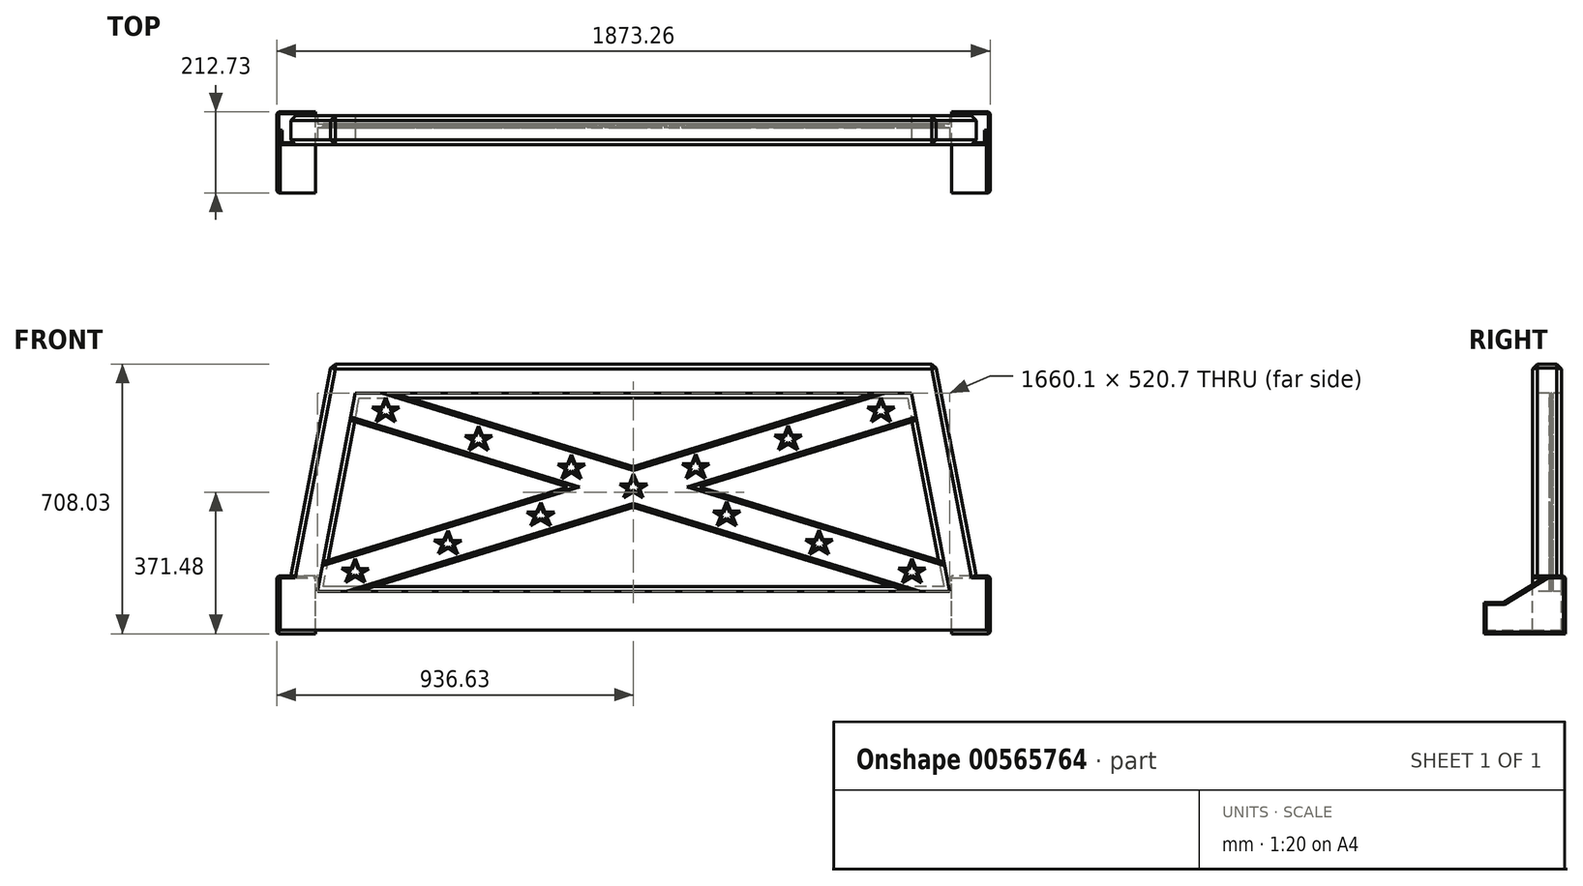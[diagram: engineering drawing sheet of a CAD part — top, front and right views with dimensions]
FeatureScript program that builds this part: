
annotation { "Feature Type Name" : "Feature", "Feature Type Description" : "" }
export const myFeature = defineFeature(function(context is Context, id is Id, definition is map)
    precondition{}
    {
        {
            var Q0;
            Q0=qCreatedBy(makeId("Front.planeOp"),FACE);
            var sketch = newSketch(context, id + "F0", { "sketchPlane" : qUnion([Q0])});
            skLineSegment(sketch, "E0", {"start": v(0, 0) * mm, "end": v(1854.2, 0) * mm});
            skLineSegment(sketch, "E1", {"start": v(0, 0) * mm, "end": v(133.8, 698.5) * mm});
            skLineSegment(sketch, "E2", {"start": v(1854.2, 0) * mm, "end": v(1720.4, 698.5) * mm});
            skLineSegment(sketch, "E3", {"start": v(133.8, 698.5) * mm, "end": v(1720.4, 698.5) * mm});
            skSolve(sketch);
        }
        {
            var Q0;
            Q0=makeQuery(id+"F0.imprint","IMPRINT",FACE,{"disambiguationData":[TD([[makeQuery(id+"F0.imprint","IMPRINT",EDGE,{"derivedFrom":sQuery(id+"F0.wireOp",EDGE,"E0")}),1.0]])]});
            var Q1;
            Q1 = qSketchRegion(id + "F2", true);
            extrude(context, id + "F1", {"entities" : qUnion([Q0, Q1]), "depth" : 76.2 * mm, "offsetDistance" : 25.4 * mm});
        }
        {
            var Q0;
            Q0=qCreatedBy(makeId("Front.planeOp"),FACE);
            var sketch = newSketch(context, id + "F2", { "sketchPlane" : qUnion([Q0])});
            skLineSegment(sketch, "E4.bottom", {"start": v(-9.53, -9.53) * mm, "end": v(92.08, -9.53) * mm});
            skLineSegment(sketch, "E4.top", {"start": v(-9.53, 142.88) * mm, "end": v(92.07, 142.88) * mm});
            skLineSegment(sketch, "E4.left", {"start": v(-9.52, -9.53) * mm, "end": v(-9.53, 142.88) * mm});
            skLineSegment(sketch, "E4.right", {"start": v(92.08, -9.53) * mm, "end": v(92.07, 142.88) * mm});
            skLineSegment(sketch, "E5.bottom", {"start": v(1863.73, -9.52) * mm, "end": v(1762.13, -9.52) * mm});
            skLineSegment(sketch, "E5.top", {"start": v(1863.73, 142.88) * mm, "end": v(1762.13, 142.88) * mm});
            skLineSegment(sketch, "E5.left", {"start": v(1863.73, -9.52) * mm, "end": v(1863.73, 142.88) * mm});
            skLineSegment(sketch, "E5.right", {"start": v(1762.13, -9.52) * mm, "end": v(1762.13, 142.88) * mm});
            skSolve(sketch);
        }
        {
            var Q0;
            Q0 = qSketchRegion(id + "F2", true);
            extrude(context, id + "F3", {"entities" : qUnion([Q0]), "operationType" : NewBodyOperationType.ADD, "oppositeDirection" : true, "depth" : 9.52 * mm, "offsetDistance" : 25.4 * mm});
        }
        {
            var Q0;
            Q0=qCreatedBy(makeId("Front.planeOp"),FACE);
            var sketch = newSketch(context, id + "F4", { "sketchPlane" : qUnion([Q0])});
            skLineSegment(sketch, "E6", {"start": v(92.08, 0) * mm, "end": v(92.08, -9.53) * mm});
            skLineSegment(sketch, "E7", {"start": v(92.08, -9.53) * mm, "end": v(-9.52, -9.53) * mm});
            skLineSegment(sketch, "E8", {"start": v(-9.52, -9.53) * mm, "end": v(-9.52, 142.87) * mm});
            skLineSegment(sketch, "E9", {"start": v(-9.52, 142.87) * mm, "end": v(0, 142.87) * mm});
            skLineSegment(sketch, "E10", {"start": v(0, 142.87) * mm, "end": v(0, 0) * mm});
            skLineSegment(sketch, "E11", {"start": v(0, 0) * mm, "end": v(92.08, 0) * mm});
            skLineSegment(sketch, "E12", {"start": v(1863.73, -9.52) * mm, "end": v(1863.73, 142.88) * mm});
            skLineSegment(sketch, "E13", {"start": v(1863.73, 142.88) * mm, "end": v(1854.2, 142.88) * mm});
            skLineSegment(sketch, "E14", {"start": v(1854.2, 142.88) * mm, "end": v(1854.2, 0) * mm});
            skLineSegment(sketch, "E15", {"start": v(1854.2, 0) * mm, "end": v(1762.13, 0) * mm});
            skLineSegment(sketch, "E16", {"start": v(1762.13, 0) * mm, "end": v(1762.13, -9.53) * mm});
            skLineSegment(sketch, "E17", {"start": v(1762.13, -9.53) * mm, "end": v(1863.73, -9.52) * mm});
            skSolve(sketch);
        }
        {
            var Q0;
            Q0 = qSketchRegion(id + "F4", true);
            var Q1;
            Q1 = qSketchRegion(id + "F6", true);
            extrude(context, id + "F5", {"entities" : qUnion([Q0, Q1]), "operationType" : NewBodyOperationType.ADD, "depth" : 152.4 * mm, "offsetDistance" : 25.4 * mm});
        }
        {
            var Q0;
            Q0=qCreatedBy(makeId("Right.planeOp"),FACE);
            var sketch = newSketch(context, id + "F6", { "sketchPlane" : qUnion([Q0])});
            skLineSegment(sketch, "E18", {"start": v(-38.1, 142.88) * mm, "end": v(-152.4, 73.02) * mm});
            skLineSegment(sketch, "E19", {"start": v(-152.4, 73.02) * mm, "end": v(-152.4, 142.88) * mm});
            skLineSegment(sketch, "E20", {"start": v(-152.4, 142.88) * mm, "end": v(-38.1, 142.88) * mm});
            skSolve(sketch);
        }
        {
            var Q0;
            Q0 = qSketchRegion(id + "F6", true);
            extrude(context, id + "F7", {"entities" : qUnion([Q0]), "operationType" : NewBodyOperationType.REMOVE, "oppositeDirection" : true, "depth" : 9.52 * mm, "offsetDistance" : 25.4 * mm});
        }
        {
            var Q0;
            Q0=makeQuery(id+"F5.opExtrude","SWEPT_FACE",FACE,{"disambiguationData":[OSD([sQuery(id+"F4.wireOp",EDGE,"E14")])]});
            var sketch = newSketch(context, id + "F8", { "sketchPlane" : qUnion([Q0])});
            skLineSegment(sketch, "E21", {"start": v(38.1, 142.87) * mm, "end": v(152.4, 73.02) * mm});
            skLineSegment(sketch, "E22", {"start": v(152.4, 73.02) * mm, "end": v(152.4, 142.87) * mm});
            skLineSegment(sketch, "E23", {"start": v(152.4, 142.87) * mm, "end": v(38.1, 142.87) * mm});
            skSolve(sketch);
        }
        {
            var Q0;
            Q0 = qSketchRegion(id + "F8", true);
            extrude(context, id + "F9", {"entities" : qUnion([Q0]), "operationType" : NewBodyOperationType.REMOVE, "oppositeDirection" : true, "depth" : 9.52 * mm, "offsetDistance" : 25.4 * mm});
        }
        {
            var Q0;
            Q0=makeQuery(id+"F5.opExtrude","CAP_FACE",FACE,{"disambiguationData":[OSD([sQuery(id+"F4.wireOp",EDGE,"E12"),sQuery(id+"F4.wireOp",EDGE,"E13"),sQuery(id+"F4.wireOp",EDGE,"E14"),sQuery(id+"F4.wireOp",EDGE,"E15"),sQuery(id+"F4.wireOp",EDGE,"E16"),sQuery(id+"F4.wireOp",EDGE,"E17")])],"isStart":false});
            var sketch = newSketch(context, id + "F10", { "sketchPlane" : qUnion([Q0])});
            skLineSegment(sketch, "E24", {"start": v(1762.13, -9.53) * mm, "end": v(1863.73, -9.52) * mm});
            skLineSegment(sketch, "E25", {"start": v(1863.73, -9.52) * mm, "end": v(1863.73, 73.03) * mm});
            skLineSegment(sketch, "E26", {"start": v(1863.73, 73.03) * mm, "end": v(1854.2, 73.03) * mm});
            skLineSegment(sketch, "E27", {"start": v(1854.2, 73.03) * mm, "end": v(1854.2, 0) * mm});
            skLineSegment(sketch, "E28", {"start": v(1854.2, 0) * mm, "end": v(1762.13, 0) * mm});
            skLineSegment(sketch, "E29", {"start": v(1762.13, 0) * mm, "end": v(1762.13, -9.53) * mm});
            skSolve(sketch);
        }
        {
            var Q0;
            Q0 = qSketchRegion(id + "F10", true);
            var Q1;
            Q1 = qSketchRegion(id + "F12", true);
            extrude(context, id + "F11", {"entities" : qUnion([Q0, Q1]), "operationType" : NewBodyOperationType.ADD, "depth" : 50.8 * mm, "offsetDistance" : 25.4 * mm});
        }
        {
            var Q0;
            Q0=makeQuery(id+"F5.opExtrude","CAP_FACE",FACE,{"disambiguationData":[OSD([sQuery(id+"F4.wireOp",EDGE,"E6"),sQuery(id+"F4.wireOp",EDGE,"E7"),sQuery(id+"F4.wireOp",EDGE,"E8"),sQuery(id+"F4.wireOp",EDGE,"E9"),sQuery(id+"F4.wireOp",EDGE,"E10"),sQuery(id+"F4.wireOp",EDGE,"E11")])],"isStart":false});
            var sketch = newSketch(context, id + "F12", { "sketchPlane" : qUnion([Q0])});
            skLineSegment(sketch, "E30", {"start": v(-9.52, 73.02) * mm, "end": v(0, 73.02) * mm});
            skLineSegment(sketch, "E31", {"start": v(0, 73.02) * mm, "end": v(0, 0) * mm});
            skLineSegment(sketch, "E32", {"start": v(0, 0) * mm, "end": v(92.08, 0) * mm});
            skLineSegment(sketch, "E33", {"start": v(92.08, 0) * mm, "end": v(92.08, -9.53) * mm});
            skLineSegment(sketch, "E34", {"start": v(92.08, -9.53) * mm, "end": v(-9.52, -9.53) * mm});
            skLineSegment(sketch, "E35", {"start": v(-9.52, -9.52) * mm, "end": v(-9.52, 73.02) * mm});
            skSolve(sketch);
        }
        {
            var Q0;
            Q0 = qSketchRegion(id + "F12", true);
            extrude(context, id + "F13", {"entities" : qUnion([Q0]), "operationType" : NewBodyOperationType.ADD, "depth" : 50.8 * mm, "offsetDistance" : 25.4 * mm});
        }
        {
            var Q0;
            Q0=makeQuery(id+"F1.opExtrude","CAP_FACE",FACE,{"disambiguationData":[OSD([sQuery(id+"F0.wireOp",EDGE,"E0"),sQuery(id+"F0.wireOp",EDGE,"E1"),sQuery(id+"F0.wireOp",EDGE,"E2"),sQuery(id+"F0.wireOp",EDGE,"E3")])],"isStart":false});
            var sketch = newSketch(context, id + "F14", { "sketchPlane" : qUnion([Q0])});
            skLineSegment(sketch, "E36", {"start": v(97.05, 101.6) * mm, "end": v(196.8, 622.3) * mm});
            skLineSegment(sketch, "E37", {"start": v(196.8, 622.3) * mm, "end": v(1657.4, 622.3) * mm});
            skLineSegment(sketch, "E38", {"start": v(1657.4, 622.3) * mm, "end": v(1757.15, 101.6) * mm});
            skLineSegment(sketch, "E39", {"start": v(1757.15, 101.6) * mm, "end": v(97.05, 101.6) * mm});
            skSolve(sketch);
        }
        {
            var Q0;
            Q0=makeQuery(id+"F14.imprint","IMPRINT",FACE,{"disambiguationData":[TD([[makeQuery(id+"F14.imprint","IMPRINT",EDGE,{"derivedFrom":sQuery(id+"F14.wireOp",EDGE,"E36")}),-1.0]])]});
            extrude(context, id + "F15", {"entities" : qUnion([Q0]), "operationType" : NewBodyOperationType.REMOVE, "oppositeDirection" : true, "depth" : 76.2 * mm, "offsetDistance" : 25.4 * mm});
        }
        {
            var Q0;
            Q0=makeQuery(id+"F1.opExtrude","CAP_FACE",FACE,{"disambiguationData":[OSD([sQuery(id+"F0.wireOp",EDGE,"E0"),sQuery(id+"F0.wireOp",EDGE,"E1"),sQuery(id+"F0.wireOp",EDGE,"E2"),sQuery(id+"F0.wireOp",EDGE,"E3")])],"isStart":false});
            cPlane(context, id + "F16", {"entities" : qUnion([Q0]), "cplaneType" : CPlaneType.OFFSET, "offset" : 50.8 * mm, "oppositeDirection" : true, "width" : 152.4 * mm, "height" : 152.4 * mm});
        }
        {
            var Q0;
            Q0=qCreatedBy(id+"F16.planeOp",FACE);
            var sketch = newSketch(context, id + "F17", { "sketchPlane" : qUnion([Q0])});
            skLineSegment(sketch, "E40", {"start": v(97.05, 101.6) * mm, "end": v(196.8, 622.3) * mm});
            skLineSegment(sketch, "E41", {"start": v(196.8, 622.3) * mm, "end": v(1657.4, 622.3) * mm});
            skLineSegment(sketch, "E42", {"start": v(1657.4, 622.3) * mm, "end": v(1757.15, 101.6) * mm});
            skLineSegment(sketch, "E43", {"start": v(1757.15, 101.6) * mm, "end": v(97.05, 101.6) * mm});
            skLineSegment(sketch, "E44", {"start": v(112.41, 114.3) * mm, "end": v(207.29, 609.6) * mm});
            skLineSegment(sketch, "E45", {"start": v(207.29, 609.6) * mm, "end": v(1646.91, 609.6) * mm});
            skLineSegment(sketch, "E46", {"start": v(1646.91, 609.6) * mm, "end": v(1741.79, 114.3) * mm});
            skLineSegment(sketch, "E47", {"start": v(1741.79, 114.3) * mm, "end": v(112.41, 114.3) * mm});
            skSolve(sketch);
        }
        {
            var Q0;
            Q0 = qSketchRegion(id + "F17", true);
            extrude(context, id + "F18", {"entities" : qUnion([Q0]), "operationType" : NewBodyOperationType.ADD, "oppositeDirection" : true, "depth" : 3.17 * mm, "offsetDistance" : 25.4 * mm});
        }
        {
            var Q0;
            Q0=qCreatedBy(id+"F16.planeOp",FACE);
            var sketch = newSketch(context, id + "F19", { "sketchPlane" : qUnion([Q0])});
            skLineSegment(sketch, "E48", {"start": v(97.05, 101.6) * mm, "end": v(196.8, 622.3) * mm});
            skLineSegment(sketch, "E49", {"start": v(196.8, 622.3) * mm, "end": v(1657.4, 622.3) * mm});
            skLineSegment(sketch, "E50", {"start": v(1657.4, 622.3) * mm, "end": v(1757.15, 101.6) * mm});
            skLineSegment(sketch, "E51", {"start": v(1757.15, 101.6) * mm, "end": v(97.05, 101.6) * mm});
            skSolve(sketch);
        }
        {
            var Q0;
            Q0=qCreatedBy(id+"F16.planeOp",FACE);
            var sketch = newSketch(context, id + "F20", { "sketchPlane" : qUnion([Q0])});
            skLineSegment(sketch, "E52", {"start": v(196.8, 622.3) * mm, "end": v(97.05, 101.6) * mm});
            skLineSegment(sketch, "E53", {"start": v(97.05, 101.6) * mm, "end": v(1757.15, 101.6) * mm});
            skLineSegment(sketch, "E54", {"start": v(1757.15, 101.6) * mm, "end": v(1657.4, 622.3) * mm});
            skLineSegment(sketch, "E55", {"start": v(1657.4, 622.3) * mm, "end": v(196.8, 622.3) * mm});
            skSolve(sketch);
        }
        {
            var Q0;
            Q0 = qSketchRegion(id + "F20", true);
            var Q1;
            Q1 = qSketchRegion(id + "FLFXTix34sU0pSf_1", true);
            extrude(context, id + "F21", {"entities" : qUnion([Q0, Q1]), "operationType" : NewBodyOperationType.ADD, "depth" : 3.17 * mm, "offsetDistance" : 25.4 * mm});
        }
        {
            var Q0;
            Q0=makeQuery(id+"F21.opExtrude","CAP_FACE",FACE,{"disambiguationData":[OSD([sQuery(id+"F20.wireOp",EDGE,"E52"),sQuery(id+"F20.wireOp",EDGE,"E53"),sQuery(id+"F20.wireOp",EDGE,"E54"),sQuery(id+"F20.wireOp",EDGE,"E55")])],"isStart":false});
            var sketch = newSketch(context, id + "F22", { "sketchPlane" : qUnion([Q0])});
            skLineSegment(sketch, "E56", {"start": v(183.2, 551.37) * mm, "end": v(753.9, 376.28) * mm});
            skLineSegment(sketch, "E57", {"start": v(298.4, 622.3) * mm, "end": v(927.1, 429.41) * mm});
            skLineSegment(sketch, "E58", {"start": v(111.94, 179.32) * mm, "end": v(753.9, 376.28) * mm});
            skLineSegment(sketch, "E59", {"start": v(205, 101.6) * mm, "end": v(927.1, 323.14) * mm});
            skLineSegment(sketch, "E60.trimOffspring", {"start": v(927.1, 429.41) * mm, "end": v(1555.8, 622.3) * mm});
            skLineSegment(sketch, "E61.trimOffspring", {"start": v(1100.3, 376.28) * mm, "end": v(1742.26, 179.32) * mm});
            skLineSegment(sketch, "E62.trimOffspring", {"start": v(1100.3, 376.28) * mm, "end": v(1671, 551.37) * mm});
            skLineSegment(sketch, "E63.trimOffspring", {"start": v(927.1, 323.14) * mm, "end": v(1649.2, 101.6) * mm});
            skSolve(sketch);
        }
        {
            var Q0;
            {var subQ0=sQuery(id+"F22.wireOp",EDGE,"E56");Q0=makeQuery(id+"F22.imprint","IMPRINT",FACE,{"disambiguationData":[TD([[makeQuery(id+"F22.imprint","IMPRINT",EDGE,{"derivedFrom":subQ0}),-1.0]])]});}
            var Q1;
            {var subQ0=sQuery(id+"F22.wireOp",EDGE,"E57");Q1=makeQuery(id+"F22.imprint","IMPRINT",FACE,{"disambiguationData":[TD([[makeQuery(id+"F22.imprint","IMPRINT",EDGE,{"derivedFrom":subQ0}),1.0]])]});}
            var Q2;
            {var subQ0=sQuery(id+"F22.wireOp",EDGE,"E61.trimOffspring");Q2=makeQuery(id+"F22.imprint","IMPRINT",FACE,{"disambiguationData":[TD([[makeQuery(id+"F22.imprint","IMPRINT",EDGE,{"derivedFrom":subQ0}),1.0]])]});}
            var Q3;
            {var subQ0=sQuery(id+"F22.wireOp",EDGE,"E59");Q3=makeQuery(id+"F22.imprint","IMPRINT",FACE,{"disambiguationData":[TD([[makeQuery(id+"F22.imprint","IMPRINT",EDGE,{"derivedFrom":subQ0}),-1.0]])]});}
            extrude(context, id + "F23", {"entities" : qUnion([Q0, Q1, Q2, Q3]), "operationType" : NewBodyOperationType.REMOVE, "oppositeDirection" : true, "depth" : 3.17 * mm, "offsetDistance" : 25.4 * mm});
        }
        {
            var Q0;
            Q0=makeQuery(id+"F21.opExtrude","CAP_FACE",FACE,{"disambiguationData":[OSD([sQuery(id+"F20.wireOp",EDGE,"E52"),sQuery(id+"F20.wireOp",EDGE,"E53"),sQuery(id+"F20.wireOp",EDGE,"E54"),sQuery(id+"F20.wireOp",EDGE,"E55")])],"isStart":false});
            var sketch = newSketch(context, id + "F24", { "sketchPlane" : qUnion([Q0])});
            skLineSegment(sketch, "E64", {"start": v(184.4, 557.64) * mm, "end": v(775.55, 376.28) * mm});
            skLineSegment(sketch, "E65", {"start": v(775.55, 376.28) * mm, "end": v(110.58, 172.27) * mm});
            skLineSegment(sketch, "E66", {"start": v(183.35, 101.6) * mm, "end": v(927.1, 329.78) * mm});
            skLineSegment(sketch, "E67", {"start": v(927.1, 329.78) * mm, "end": v(1670.85, 101.6) * mm});
            skLineSegment(sketch, "E68", {"start": v(276.74, 622.3) * mm, "end": v(927.1, 422.77) * mm});
            skLineSegment(sketch, "E69", {"start": v(927.1, 422.77) * mm, "end": v(1577.46, 622.3) * mm});
            skLineSegment(sketch, "E70", {"start": v(1669.8, 557.64) * mm, "end": v(1078.65, 376.28) * mm});
            skLineSegment(sketch, "E71", {"start": v(1078.65, 376.28) * mm, "end": v(1743.62, 172.27) * mm});
            skSolve(sketch);
        }
        {
            var Q0;
            {var subQ30=sQuery(id+"F24.wireOp",EDGE,"E64");Q0=makeQuery(id+"F24.imprint","IMPRINT",FACE,{"disambiguationData":[TD([[makeQuery(id+"F24.imprint","IMPRINT",EDGE,{"derivedFrom":subQ30}),1.0]])]});}
            extrude(context, id + "F25", {"entities" : qUnion([Q0]), "operationType" : NewBodyOperationType.ADD, "depth" : 3.17 * mm, "offsetDistance" : 25.4 * mm});
        }
        {
            var Q0;
            Q0=makeQuery(id+"F25.opExtrude","CAP_FACE",FACE,{"disambiguationData":[OSD([sQuery(id+"F20.wireOp",EDGE,"E52"),sQuery(id+"F20.wireOp",EDGE,"E53"),sQuery(id+"F20.wireOp",EDGE,"E54"),sQuery(id+"F20.wireOp",EDGE,"E55"),sQuery(id+"F24.wireOp",EDGE,"E64"),sQuery(id+"F24.wireOp",EDGE,"E65"),sQuery(id+"F24.wireOp",EDGE,"E66"),sQuery(id+"F24.wireOp",EDGE,"E67"),sQuery(id+"F24.wireOp",EDGE,"E68"),sQuery(id+"F24.wireOp",EDGE,"E69"),sQuery(id+"F24.wireOp",EDGE,"E70"),sQuery(id+"F24.wireOp",EDGE,"E71")])],"isStart":false});
            var sketch = newSketch(context, id + "F26", { "sketchPlane" : qUnion([Q0])});
            skLineSegment(sketch, "E72", {"start": v(241.55, 585.93) * mm, "end": v(266.95, 585.93) * mm});
            skLineSegment(sketch, "E73", {"start": v(312.67, 585.93) * mm, "end": v(292.35, 573.23) * mm});
            skLineSegment(sketch, "E74", {"start": v(251.7, 547.83) * mm, "end": v(261.87, 573.23) * mm});
            skLineSegment(sketch, "E75", {"start": v(277.1, 611.33) * mm, "end": v(287.27, 585.93) * mm});
            skLineSegment(sketch, "E76", {"start": v(302.5, 547.83) * mm, "end": v(277.1, 563.7) * mm});
            skLineSegment(sketch, "E77.trimOffspring", {"start": v(266.95, 585.93) * mm, "end": v(277.1, 611.33) * mm});
            skLineSegment(sketch, "E78.trimOffspring", {"start": v(287.27, 585.93) * mm, "end": v(312.67, 585.93) * mm});
            skLineSegment(sketch, "E79.trimOffspring", {"start": v(292.35, 573.23) * mm, "end": v(302.5, 547.83) * mm});
            skLineSegment(sketch, "E80.trimOffspring", {"start": v(277.1, 563.7) * mm, "end": v(251.7, 547.83) * mm});
            skLineSegment(sketch, "E81.trimOffspring", {"start": v(261.87, 573.23) * mm, "end": v(241.55, 585.93) * mm});
            skLineSegment(sketch, "E82.1.0.0", {"start": v(556, 511.05) * mm, "end": v(535.69, 498.35) * mm});
            skLineSegment(sketch, "E82.1.0.1", {"start": v(530.6, 511.05) * mm, "end": v(556, 511.05) * mm});
            skLineSegment(sketch, "E82.1.0.2", {"start": v(520.45, 536.45) * mm, "end": v(530.6, 511.05) * mm});
            skLineSegment(sketch, "E82.1.0.3", {"start": v(510.29, 511.05) * mm, "end": v(520.45, 536.45) * mm});
            skLineSegment(sketch, "E82.1.0.4", {"start": v(484.89, 511.05) * mm, "end": v(510.29, 511.05) * mm});
            skLineSegment(sketch, "E82.1.0.5", {"start": v(505.2, 498.35) * mm, "end": v(484.89, 511.05) * mm});
            skLineSegment(sketch, "E82.1.0.6", {"start": v(535.69, 498.35) * mm, "end": v(545.85, 472.95) * mm});
            skLineSegment(sketch, "E82.1.0.7", {"start": v(545.85, 472.95) * mm, "end": v(520.45, 488.82) * mm});
            skLineSegment(sketch, "E82.1.0.8", {"start": v(520.45, 488.82) * mm, "end": v(495.05, 472.95) * mm});
            skLineSegment(sketch, "E82.1.0.9", {"start": v(495.05, 472.95) * mm, "end": v(505.2, 498.35) * mm});
            skLineSegment(sketch, "E82.2.0.0", {"start": v(799.34, 436.16) * mm, "end": v(779.02, 423.46) * mm});
            skLineSegment(sketch, "E82.2.0.1", {"start": v(773.94, 436.16) * mm, "end": v(799.34, 436.16) * mm});
            skLineSegment(sketch, "E82.2.0.2", {"start": v(763.78, 461.56) * mm, "end": v(773.94, 436.16) * mm});
            skLineSegment(sketch, "E82.2.0.3", {"start": v(753.62, 436.16) * mm, "end": v(763.78, 461.56) * mm});
            skLineSegment(sketch, "E82.2.0.4", {"start": v(728.22, 436.16) * mm, "end": v(753.62, 436.16) * mm});
            skLineSegment(sketch, "E82.2.0.5", {"start": v(748.54, 423.46) * mm, "end": v(728.22, 436.16) * mm});
            skLineSegment(sketch, "E82.2.0.6", {"start": v(779.02, 423.46) * mm, "end": v(789.18, 398.06) * mm});
            skLineSegment(sketch, "E82.2.0.7", {"start": v(789.18, 398.06) * mm, "end": v(763.78, 413.94) * mm});
            skLineSegment(sketch, "E82.2.0.8", {"start": v(763.78, 413.94) * mm, "end": v(738.38, 398.06) * mm});
            skLineSegment(sketch, "E82.2.0.9", {"start": v(738.38, 398.06) * mm, "end": v(748.54, 423.46) * mm});
            skLineSegment(sketch, "E82.direction1", {"start": v(292.35, 573.23) * mm, "end": v(535.69, 498.35) * mm, "construction": true});
            skLineSegment(sketch, "E83.2.0.0", {"start": v(232.58, 161.52) * mm, "end": v(212.63, 149.52) * mm});
            skLineSegment(sketch, "E83.2.0.1", {"start": v(207.18, 161.52) * mm, "end": v(232.58, 161.52) * mm});
            skLineSegment(sketch, "E83.2.0.2", {"start": v(196.66, 187.82) * mm, "end": v(207.18, 161.52) * mm});
            skLineSegment(sketch, "E83.2.0.3", {"start": v(185.78, 162.2) * mm, "end": v(196.66, 187.82) * mm});
            skLineSegment(sketch, "E83.2.0.4", {"start": v(160.38, 162.2) * mm, "end": v(185.78, 162.2) * mm});
            skLineSegment(sketch, "E83.2.0.5", {"start": v(181.19, 149.52) * mm, "end": v(160.38, 162.2) * mm});
            skLineSegment(sketch, "E83.2.0.6", {"start": v(212.63, 149.52) * mm, "end": v(222.06, 125.93) * mm});
            skLineSegment(sketch, "E83.2.0.7", {"start": v(222.06, 125.93) * mm, "end": v(196.66, 141.42) * mm});
            skLineSegment(sketch, "E83.2.0.8", {"start": v(196.66, 141.42) * mm, "end": v(171.26, 126.14) * mm});
            skLineSegment(sketch, "E83.2.0.9", {"start": v(171.26, 126.14) * mm, "end": v(181.19, 149.52) * mm});
            skLineSegment(sketch, "E84.1.0.0", {"start": v(429.26, 236.22) * mm, "end": v(440.14, 261.84) * mm});
            skLineSegment(sketch, "E84.1.0.1", {"start": v(450.66, 235.54) * mm, "end": v(476.06, 235.54) * mm});
            skLineSegment(sketch, "E84.1.0.2", {"start": v(440.14, 261.84) * mm, "end": v(450.66, 235.54) * mm});
            skLineSegment(sketch, "E84.1.0.3", {"start": v(476.06, 235.54) * mm, "end": v(456.1, 223.54) * mm});
            skLineSegment(sketch, "E84.1.0.4", {"start": v(456.1, 223.54) * mm, "end": v(465.54, 199.95) * mm});
            skLineSegment(sketch, "E84.1.0.5", {"start": v(465.54, 199.95) * mm, "end": v(440.14, 215.44) * mm});
            skLineSegment(sketch, "E84.1.0.6", {"start": v(440.14, 215.44) * mm, "end": v(414.74, 200.16) * mm});
            skLineSegment(sketch, "E84.1.0.7", {"start": v(414.74, 200.16) * mm, "end": v(424.67, 223.54) * mm});
            skLineSegment(sketch, "E84.1.0.8", {"start": v(424.67, 223.54) * mm, "end": v(403.86, 236.22) * mm});
            skLineSegment(sketch, "E84.1.0.9", {"start": v(403.86, 236.22) * mm, "end": v(429.26, 236.22) * mm});
            skLineSegment(sketch, "E84.2.0.0", {"start": v(672.74, 310.24) * mm, "end": v(683.62, 335.86) * mm});
            skLineSegment(sketch, "E84.2.0.1", {"start": v(694.14, 309.56) * mm, "end": v(719.54, 309.56) * mm});
            skLineSegment(sketch, "E84.2.0.2", {"start": v(683.62, 335.86) * mm, "end": v(694.14, 309.56) * mm});
            skLineSegment(sketch, "E84.2.0.3", {"start": v(719.54, 309.56) * mm, "end": v(699.59, 297.56) * mm});
            skLineSegment(sketch, "E84.2.0.4", {"start": v(699.59, 297.56) * mm, "end": v(709.02, 273.97) * mm});
            skLineSegment(sketch, "E84.2.0.5", {"start": v(709.02, 273.97) * mm, "end": v(683.62, 289.46) * mm});
            skLineSegment(sketch, "E84.2.0.6", {"start": v(683.62, 289.46) * mm, "end": v(658.22, 274.18) * mm});
            skLineSegment(sketch, "E84.2.0.7", {"start": v(658.22, 274.18) * mm, "end": v(668.15, 297.56) * mm});
            skLineSegment(sketch, "E84.2.0.8", {"start": v(668.15, 297.56) * mm, "end": v(647.34, 310.24) * mm});
            skLineSegment(sketch, "E84.2.0.9", {"start": v(647.34, 310.24) * mm, "end": v(672.74, 310.24) * mm});
            skLineSegment(sketch, "E84.3.0.0", {"start": v(916.22, 384.26) * mm, "end": v(927.1, 409.88) * mm});
            skLineSegment(sketch, "E84.3.0.1", {"start": v(937.62, 383.58) * mm, "end": v(963.02, 383.58) * mm});
            skLineSegment(sketch, "E84.3.0.2", {"start": v(927.1, 409.88) * mm, "end": v(937.62, 383.58) * mm});
            skLineSegment(sketch, "E84.3.0.3", {"start": v(963.02, 383.58) * mm, "end": v(943.07, 371.58) * mm});
            skLineSegment(sketch, "E84.3.0.4", {"start": v(943.07, 371.58) * mm, "end": v(952.5, 348) * mm});
            skLineSegment(sketch, "E84.3.0.5", {"start": v(952.5, 348) * mm, "end": v(927.1, 363.48) * mm});
            skLineSegment(sketch, "E84.3.0.6", {"start": v(927.1, 363.48) * mm, "end": v(901.7, 348.2) * mm});
            skLineSegment(sketch, "E84.3.0.7", {"start": v(901.7, 348.2) * mm, "end": v(911.63, 371.58) * mm});
            skLineSegment(sketch, "E84.3.0.8", {"start": v(911.63, 371.58) * mm, "end": v(890.82, 384.26) * mm});
            skLineSegment(sketch, "E84.3.0.9", {"start": v(890.82, 384.26) * mm, "end": v(916.22, 384.26) * mm});
            skLineSegment(sketch, "E84.direction1", {"start": v(185.78, 162.2) * mm, "end": v(429.26, 236.22) * mm, "construction": true});
            skLineSegment(sketch, "E85.2.0.0", {"start": v(1612.65, 585.94) * mm, "end": v(1592.33, 573.24) * mm});
            skLineSegment(sketch, "E85.2.0.1", {"start": v(1587.25, 585.94) * mm, "end": v(1612.65, 585.94) * mm});
            skLineSegment(sketch, "E85.2.0.2", {"start": v(1577.09, 611.34) * mm, "end": v(1587.25, 585.94) * mm});
            skLineSegment(sketch, "E85.2.0.3", {"start": v(1566.93, 585.94) * mm, "end": v(1577.09, 611.34) * mm});
            skLineSegment(sketch, "E85.2.0.4", {"start": v(1541.53, 585.94) * mm, "end": v(1566.93, 585.94) * mm});
            skLineSegment(sketch, "E85.2.0.5", {"start": v(1561.85, 573.24) * mm, "end": v(1541.53, 585.94) * mm});
            skLineSegment(sketch, "E85.2.0.6", {"start": v(1592.33, 573.24) * mm, "end": v(1602.49, 547.84) * mm});
            skLineSegment(sketch, "E85.2.0.7", {"start": v(1602.49, 547.84) * mm, "end": v(1577.09, 563.72) * mm});
            skLineSegment(sketch, "E85.2.0.8", {"start": v(1577.09, 563.72) * mm, "end": v(1551.69, 547.84) * mm});
            skLineSegment(sketch, "E85.2.0.9", {"start": v(1551.69, 547.84) * mm, "end": v(1561.85, 573.24) * mm});
            skLineSegment(sketch, "E86.2.0.0", {"start": v(1693.82, 162.2) * mm, "end": v(1673.5, 149.5) * mm});
            skLineSegment(sketch, "E86.2.0.1", {"start": v(1668.42, 162.2) * mm, "end": v(1693.82, 162.2) * mm});
            skLineSegment(sketch, "E86.2.0.2", {"start": v(1658.26, 187.6) * mm, "end": v(1668.42, 162.2) * mm});
            skLineSegment(sketch, "E86.2.0.3", {"start": v(1648.1, 162.2) * mm, "end": v(1658.26, 187.6) * mm});
            skLineSegment(sketch, "E86.2.0.4", {"start": v(1622.7, 162.2) * mm, "end": v(1648.1, 162.2) * mm});
            skLineSegment(sketch, "E86.2.0.5", {"start": v(1643.02, 149.5) * mm, "end": v(1622.7, 162.2) * mm});
            skLineSegment(sketch, "E86.2.0.6", {"start": v(1673.5, 149.5) * mm, "end": v(1683.66, 124.1) * mm});
            skLineSegment(sketch, "E86.2.0.7", {"start": v(1683.66, 124.1) * mm, "end": v(1658.26, 139.98) * mm});
            skLineSegment(sketch, "E86.2.0.8", {"start": v(1658.26, 139.98) * mm, "end": v(1632.86, 124.1) * mm});
            skLineSegment(sketch, "E86.2.0.9", {"start": v(1632.86, 124.1) * mm, "end": v(1643.02, 149.5) * mm});
            skLineSegment(sketch, "E87.1.0.0", {"start": v(1415.1, 215.05) * mm, "end": v(1389.7, 199.17) * mm});
            skLineSegment(sketch, "E87.1.0.1", {"start": v(1440.5, 199.17) * mm, "end": v(1415.1, 215.05) * mm});
            skLineSegment(sketch, "E87.1.0.2", {"start": v(1430.34, 224.57) * mm, "end": v(1440.5, 199.17) * mm});
            skLineSegment(sketch, "E87.1.0.3", {"start": v(1450.66, 237.27) * mm, "end": v(1430.34, 224.57) * mm});
            skLineSegment(sketch, "E87.1.0.4", {"start": v(1425.26, 237.27) * mm, "end": v(1450.66, 237.27) * mm});
            skLineSegment(sketch, "E87.1.0.5", {"start": v(1415.1, 262.67) * mm, "end": v(1425.26, 237.27) * mm});
            skLineSegment(sketch, "E87.1.0.6", {"start": v(1404.94, 237.27) * mm, "end": v(1415.1, 262.67) * mm});
            skLineSegment(sketch, "E87.1.0.7", {"start": v(1379.54, 237.27) * mm, "end": v(1404.94, 237.27) * mm});
            skLineSegment(sketch, "E87.1.0.8", {"start": v(1389.7, 199.17) * mm, "end": v(1399.86, 224.57) * mm});
            skLineSegment(sketch, "E87.1.0.9", {"start": v(1399.86, 224.57) * mm, "end": v(1379.54, 237.27) * mm});
            skLineSegment(sketch, "E87.2.0.0", {"start": v(1171.94, 290.1) * mm, "end": v(1146.54, 274.23) * mm});
            skLineSegment(sketch, "E87.2.0.1", {"start": v(1197.34, 274.23) * mm, "end": v(1171.94, 290.1) * mm});
            skLineSegment(sketch, "E87.2.0.2", {"start": v(1187.18, 299.63) * mm, "end": v(1197.34, 274.23) * mm});
            skLineSegment(sketch, "E87.2.0.3", {"start": v(1207.5, 312.33) * mm, "end": v(1187.18, 299.63) * mm});
            skLineSegment(sketch, "E87.2.0.4", {"start": v(1182.1, 312.33) * mm, "end": v(1207.5, 312.33) * mm});
            skLineSegment(sketch, "E87.2.0.5", {"start": v(1171.94, 337.73) * mm, "end": v(1182.1, 312.33) * mm});
            skLineSegment(sketch, "E87.2.0.6", {"start": v(1161.78, 312.33) * mm, "end": v(1171.94, 337.73) * mm});
            skLineSegment(sketch, "E87.2.0.7", {"start": v(1136.38, 312.33) * mm, "end": v(1161.78, 312.33) * mm});
            skLineSegment(sketch, "E87.2.0.8", {"start": v(1146.54, 274.23) * mm, "end": v(1156.7, 299.63) * mm});
            skLineSegment(sketch, "E87.2.0.9", {"start": v(1156.7, 299.63) * mm, "end": v(1136.38, 312.33) * mm});
            skLineSegment(sketch, "E87.direction1", {"start": v(1632.86, 124.1) * mm, "end": v(1389.7, 199.17) * mm, "construction": true});
            skLineSegment(sketch, "E88.1.0.0", {"start": v(1333.59, 536.96) * mm, "end": v(1343.75, 511.56) * mm});
            skLineSegment(sketch, "E88.1.0.1", {"start": v(1343.75, 511.56) * mm, "end": v(1369.15, 511.56) * mm});
            skLineSegment(sketch, "E88.1.0.2", {"start": v(1369.15, 511.56) * mm, "end": v(1348.83, 498.86) * mm});
            skLineSegment(sketch, "E88.1.0.3", {"start": v(1348.83, 498.86) * mm, "end": v(1358.99, 473.46) * mm});
            skLineSegment(sketch, "E88.1.0.4", {"start": v(1358.99, 473.46) * mm, "end": v(1333.59, 489.33) * mm});
            skLineSegment(sketch, "E88.1.0.5", {"start": v(1333.59, 489.33) * mm, "end": v(1308.19, 473.46) * mm});
            skLineSegment(sketch, "E88.1.0.6", {"start": v(1308.19, 473.46) * mm, "end": v(1318.35, 498.86) * mm});
            skLineSegment(sketch, "E88.1.0.7", {"start": v(1318.35, 498.86) * mm, "end": v(1298.03, 511.56) * mm});
            skLineSegment(sketch, "E88.1.0.8", {"start": v(1298.03, 511.56) * mm, "end": v(1323.43, 511.56) * mm});
            skLineSegment(sketch, "E88.1.0.9", {"start": v(1323.43, 511.56) * mm, "end": v(1333.59, 536.96) * mm});
            skLineSegment(sketch, "E88.2.0.0", {"start": v(1090.09, 462.57) * mm, "end": v(1100.25, 437.17) * mm});
            skLineSegment(sketch, "E88.2.0.1", {"start": v(1100.25, 437.17) * mm, "end": v(1125.65, 437.17) * mm});
            skLineSegment(sketch, "E88.2.0.2", {"start": v(1125.65, 437.17) * mm, "end": v(1105.33, 424.47) * mm});
            skLineSegment(sketch, "E88.2.0.3", {"start": v(1105.33, 424.47) * mm, "end": v(1115.49, 399.07) * mm});
            skLineSegment(sketch, "E88.2.0.4", {"start": v(1115.49, 399.07) * mm, "end": v(1090.09, 414.94) * mm});
            skLineSegment(sketch, "E88.2.0.5", {"start": v(1090.09, 414.94) * mm, "end": v(1064.69, 399.07) * mm});
            skLineSegment(sketch, "E88.2.0.6", {"start": v(1064.69, 399.07) * mm, "end": v(1074.85, 424.47) * mm});
            skLineSegment(sketch, "E88.2.0.7", {"start": v(1074.85, 424.47) * mm, "end": v(1054.53, 437.17) * mm});
            skLineSegment(sketch, "E88.2.0.8", {"start": v(1054.53, 437.17) * mm, "end": v(1079.93, 437.17) * mm});
            skLineSegment(sketch, "E88.2.0.9", {"start": v(1079.93, 437.17) * mm, "end": v(1090.09, 462.57) * mm});
            skLineSegment(sketch, "E88.direction1", {"start": v(1587.25, 585.94) * mm, "end": v(1343.75, 511.56) * mm, "construction": true});
            skSolve(sketch);
        }
        {
            var Q0;
            Q0 = qSketchRegion(id + "F26", true);
            extrude(context, id + "F27", {"entities" : qUnion([Q0]), "operationType" : NewBodyOperationType.REMOVE, "oppositeDirection" : true, "depth" : 3.17 * mm, "offsetDistance" : 25.4 * mm});
        }
        {
            var Q0;
            Q0=makeQuery(id+"F1.opExtrude","CAP_EDGE",EDGE,{"disambiguationData":[OSD([sQuery(id+"F0.wireOp",EDGE,"E3")])],"isStart":false});
            var Q1;
            Q1=makeQuery(id+"F1.opExtrude","SWEPT_EDGE",EDGE,{"disambiguationData":[OSD([sQuery(id+"F0.wireOp",EDGE,"E2"),sQuery(id+"F0.wireOp",EDGE,"E3")])]});
            var Q2;
            Q2=makeQuery(id+"F1.opExtrude","SWEPT_EDGE",EDGE,{"disambiguationData":[OSD([sQuery(id+"F0.wireOp",EDGE,"E1"),sQuery(id+"F0.wireOp",EDGE,"E3")])]});
            var Q3;
            Q3=makeQuery(id+"F1.opExtrude","CAP_EDGE",EDGE,{"disambiguationData":[OSD([sQuery(id+"F0.wireOp",EDGE,"E1")])],"isStart":false});
            var Q4;
            Q4=makeQuery(id+"F5.boolean.opBoolean","SPLIT",EDGE,{"derivedFrom":makeQuery(id+"F1.opExtrude","CAP_EDGE",EDGE,{"disambiguationData":[OSD([sQuery(id+"F0.wireOp",EDGE,"E2")])],"isStart":false})});
            var Q5;
            Q5=makeQuery(id+"F15.boolean.opBoolean","COPY",EDGE,{"derivedFrom":makeQuery(id+"F15.opExtrude","CAP_EDGE",EDGE,{"disambiguationData":[OSD([sQuery(id+"F14.wireOp",EDGE,"E37")])],"isStart":true})});
            var Q6;
            Q6=makeQuery(id+"F15.boolean.opBoolean","COPY",EDGE,{"derivedFrom":makeQuery(id+"F15.opExtrude","CAP_EDGE",EDGE,{"disambiguationData":[OSD([sQuery(id+"F14.wireOp",EDGE,"E38")])],"isStart":true})});
            var Q7;
            Q7=makeQuery(id+"F15.boolean.opBoolean","COPY",EDGE,{"derivedFrom":makeQuery(id+"F15.opExtrude","CAP_EDGE",EDGE,{"disambiguationData":[OSD([sQuery(id+"F14.wireOp",EDGE,"E39")])],"isStart":true})});
            var Q8;
            Q8=makeQuery(id+"F15.boolean.opBoolean","COPY",EDGE,{"derivedFrom":makeQuery(id+"F15.opExtrude","CAP_EDGE",EDGE,{"disambiguationData":[OSD([sQuery(id+"F14.wireOp",EDGE,"E36")])],"isStart":true})});
            var Q9;
            Q9=makeQuery(id+"F1.opExtrude","CAP_EDGE",EDGE,{"disambiguationData":[OSD([sQuery(id+"F0.wireOp",EDGE,"E3")])],"isStart":true});
            var Q10;
            {var subQ0=sQuery(id+"F0.wireOp",EDGE,"E1");Q10=makeQuery(id+"F3.boolean.opBoolean","SPLIT",EDGE,{"disambiguationData":[topologyDisambiguationEdgeConnected([makeQuery(id+"F1.opExtrude","CAP_FACE",FACE,{"disambiguationData":[OSD([sQuery(id+"F0.wireOp",EDGE,"E0"),subQ0,sQuery(id+"F0.wireOp",EDGE,"E2"),sQuery(id+"F0.wireOp",EDGE,"E3")])],"isStart":true})])],"derivedFrom":makeQuery(id+"F1.opExtrude","CAP_EDGE",EDGE,{"disambiguationData":[OSD([subQ0])],"isStart":true})});}
            var Q11;
            {var subQ0=sQuery(id+"F0.wireOp",EDGE,"E2");Q11=makeQuery(id+"F3.boolean.opBoolean","SPLIT",EDGE,{"disambiguationData":[topologyDisambiguationEdgeConnected([makeQuery(id+"F1.opExtrude","CAP_FACE",FACE,{"disambiguationData":[OSD([sQuery(id+"F0.wireOp",EDGE,"E0"),sQuery(id+"F0.wireOp",EDGE,"E1"),subQ0,sQuery(id+"F0.wireOp",EDGE,"E3")])],"isStart":true})])],"derivedFrom":makeQuery(id+"F1.opExtrude","CAP_EDGE",EDGE,{"disambiguationData":[OSD([subQ0])],"isStart":true})});}
            var Q12;
            Q12=makeQuery(id+"F15.boolean.opBoolean","COPY",EDGE,{"derivedFrom":makeQuery(id+"F15.opExtrude","CAP_EDGE",EDGE,{"disambiguationData":[OSD([sQuery(id+"F14.wireOp",EDGE,"E37")])],"isStart":false})});
            var Q13;
            Q13=makeQuery(id+"F15.boolean.opBoolean","COPY",EDGE,{"derivedFrom":makeQuery(id+"F15.opExtrude","CAP_EDGE",EDGE,{"disambiguationData":[OSD([sQuery(id+"F14.wireOp",EDGE,"E38")])],"isStart":false})});
            var Q14;
            Q14=makeQuery(id+"F15.boolean.opBoolean","COPY",EDGE,{"derivedFrom":makeQuery(id+"F15.opExtrude","CAP_EDGE",EDGE,{"disambiguationData":[OSD([sQuery(id+"F14.wireOp",EDGE,"E39")])],"isStart":false})});
            var Q15;
            Q15=makeQuery(id+"F15.boolean.opBoolean","COPY",EDGE,{"derivedFrom":makeQuery(id+"F15.opExtrude","CAP_EDGE",EDGE,{"disambiguationData":[OSD([sQuery(id+"F14.wireOp",EDGE,"E36")])],"isStart":false})});
            chamfer(context, id + "F28", {"entities" : qUnion([Q0, Q1, Q2, Q3, Q4, Q5, Q6, Q7, Q8, Q9, Q10, Q11, Q12, Q13, Q14, Q15]), "width" : 12.7 * mm, "tangentPropagation" : true});
        }
        {
            var Q0;
            Q0=makeQuery(id+"F1.opExtrude","CAP_FACE",FACE,{"disambiguationData":[OSD([sQuery(id+"F0.wireOp",EDGE,"E0"),sQuery(id+"F0.wireOp",EDGE,"E1"),sQuery(id+"F0.wireOp",EDGE,"E2"),sQuery(id+"F0.wireOp",EDGE,"E3")])],"isStart":false});
            var sketch = newSketch(context, id + "F29", { "sketchPlane" : qUnion([Q0])});
            skLineSegment(sketch, "E89", {"start": v(0, 0) * mm, "end": v(35.5, 0) * mm});
            skLineSegment(sketch, "E90", {"start": v(0, 0) * mm, "end": v(0, 142.88) * mm});
            skLineSegment(sketch, "E91", {"start": v(0, 142.88) * mm, "end": v(40.3, 142.88) * mm});
            skLineSegment(sketch, "E92", {"start": v(40.3, 142.88) * mm, "end": v(40.3, 0) * mm});
            skLineSegment(sketch, "E93", {"start": v(40.3, 0) * mm, "end": v(0, 0) * mm});
            skLineSegment(sketch, "E94", {"start": v(1813.9, 142.88) * mm, "end": v(1854.2, 142.88) * mm});
            skLineSegment(sketch, "E95", {"start": v(1854.2, 142.88) * mm, "end": v(1854.2, 0) * mm});
            skLineSegment(sketch, "E96", {"start": v(1854.2, 0) * mm, "end": v(1813.9, 0) * mm});
            skLineSegment(sketch, "E97", {"start": v(1813.9, 0) * mm, "end": v(1813.9, 142.88) * mm});
            skSolve(sketch);
        }
        {
            var Q0;
            Q0 = qSketchRegion(id + "F29", true);
            extrude(context, id + "F30", {"entities" : qUnion([Q0]), "operationType" : NewBodyOperationType.ADD, "oppositeDirection" : true, "depth" : 76.2 * mm, "offsetDistance" : 25.4 * mm});
        }
        {
            var Q0;
            Q0=makeQuery(id+"F27.boolean.opBoolean","COPY",FACE,{"derivedFrom":makeQuery(id+"F27.opExtrude","CAP_FACE",FACE,{"disambiguationData":[OSD([sQuery(id+"F26.wireOp",EDGE,"E72"),sQuery(id+"F26.wireOp",EDGE,"E73"),sQuery(id+"F26.wireOp",EDGE,"E74"),sQuery(id+"F26.wireOp",EDGE,"E75"),sQuery(id+"F26.wireOp",EDGE,"E76"),sQuery(id+"F26.wireOp",EDGE,"E77.trimOffspring"),sQuery(id+"F26.wireOp",EDGE,"E78.trimOffspring"),sQuery(id+"F26.wireOp",EDGE,"E79.trimOffspring"),sQuery(id+"F26.wireOp",EDGE,"E80.trimOffspring"),sQuery(id+"F26.wireOp",EDGE,"E81.trimOffspring")])],"isStart":false})});
            var Q1;
            Q1=makeQuery(id+"F27.boolean.opBoolean","COPY",FACE,{"derivedFrom":makeQuery(id+"F27.opExtrude","CAP_FACE",FACE,{"disambiguationData":[OSD([sQuery(id+"F26.wireOp",EDGE,"E82.1.0.0"),sQuery(id+"F26.wireOp",EDGE,"E82.1.0.1"),sQuery(id+"F26.wireOp",EDGE,"E82.1.0.2"),sQuery(id+"F26.wireOp",EDGE,"E82.1.0.3"),sQuery(id+"F26.wireOp",EDGE,"E82.1.0.4"),sQuery(id+"F26.wireOp",EDGE,"E82.1.0.5"),sQuery(id+"F26.wireOp",EDGE,"E82.1.0.6"),sQuery(id+"F26.wireOp",EDGE,"E82.1.0.7"),sQuery(id+"F26.wireOp",EDGE,"E82.1.0.8"),sQuery(id+"F26.wireOp",EDGE,"E82.1.0.9")])],"isStart":false})});
            var Q2;
            Q2=makeQuery(id+"F27.boolean.opBoolean","COPY",FACE,{"derivedFrom":makeQuery(id+"F27.opExtrude","CAP_FACE",FACE,{"disambiguationData":[OSD([sQuery(id+"F26.wireOp",EDGE,"E82.2.0.0"),sQuery(id+"F26.wireOp",EDGE,"E82.2.0.1"),sQuery(id+"F26.wireOp",EDGE,"E82.2.0.2"),sQuery(id+"F26.wireOp",EDGE,"E82.2.0.3"),sQuery(id+"F26.wireOp",EDGE,"E82.2.0.4"),sQuery(id+"F26.wireOp",EDGE,"E82.2.0.5"),sQuery(id+"F26.wireOp",EDGE,"E82.2.0.6"),sQuery(id+"F26.wireOp",EDGE,"E82.2.0.7"),sQuery(id+"F26.wireOp",EDGE,"E82.2.0.8"),sQuery(id+"F26.wireOp",EDGE,"E82.2.0.9")])],"isStart":false})});
            var Q3;
            Q3=makeQuery(id+"F27.boolean.opBoolean","COPY",FACE,{"derivedFrom":makeQuery(id+"F27.opExtrude","CAP_FACE",FACE,{"disambiguationData":[OSD([sQuery(id+"F26.wireOp",EDGE,"E84.3.0.0"),sQuery(id+"F26.wireOp",EDGE,"E84.3.0.1"),sQuery(id+"F26.wireOp",EDGE,"E84.3.0.2"),sQuery(id+"F26.wireOp",EDGE,"E84.3.0.3"),sQuery(id+"F26.wireOp",EDGE,"E84.3.0.4"),sQuery(id+"F26.wireOp",EDGE,"E84.3.0.5"),sQuery(id+"F26.wireOp",EDGE,"E84.3.0.6"),sQuery(id+"F26.wireOp",EDGE,"E84.3.0.7"),sQuery(id+"F26.wireOp",EDGE,"E84.3.0.8"),sQuery(id+"F26.wireOp",EDGE,"E84.3.0.9")])],"isStart":false})});
            var Q4;
            Q4=makeQuery(id+"F27.boolean.opBoolean","COPY",FACE,{"derivedFrom":makeQuery(id+"F27.opExtrude","CAP_FACE",FACE,{"disambiguationData":[OSD([sQuery(id+"F26.wireOp",EDGE,"E88.2.0.0"),sQuery(id+"F26.wireOp",EDGE,"E88.2.0.1"),sQuery(id+"F26.wireOp",EDGE,"E88.2.0.2"),sQuery(id+"F26.wireOp",EDGE,"E88.2.0.3"),sQuery(id+"F26.wireOp",EDGE,"E88.2.0.4"),sQuery(id+"F26.wireOp",EDGE,"E88.2.0.5"),sQuery(id+"F26.wireOp",EDGE,"E88.2.0.6"),sQuery(id+"F26.wireOp",EDGE,"E88.2.0.7"),sQuery(id+"F26.wireOp",EDGE,"E88.2.0.8"),sQuery(id+"F26.wireOp",EDGE,"E88.2.0.9")])],"isStart":false})});
            var Q5;
            Q5=makeQuery(id+"F27.boolean.opBoolean","COPY",FACE,{"derivedFrom":makeQuery(id+"F27.opExtrude","CAP_FACE",FACE,{"disambiguationData":[OSD([sQuery(id+"F26.wireOp",EDGE,"E88.1.0.0"),sQuery(id+"F26.wireOp",EDGE,"E88.1.0.1"),sQuery(id+"F26.wireOp",EDGE,"E88.1.0.2"),sQuery(id+"F26.wireOp",EDGE,"E88.1.0.3"),sQuery(id+"F26.wireOp",EDGE,"E88.1.0.4"),sQuery(id+"F26.wireOp",EDGE,"E88.1.0.5"),sQuery(id+"F26.wireOp",EDGE,"E88.1.0.6"),sQuery(id+"F26.wireOp",EDGE,"E88.1.0.7"),sQuery(id+"F26.wireOp",EDGE,"E88.1.0.8"),sQuery(id+"F26.wireOp",EDGE,"E88.1.0.9")])],"isStart":false})});
            var Q6;
            Q6=makeQuery(id+"F27.boolean.opBoolean","COPY",FACE,{"derivedFrom":makeQuery(id+"F27.opExtrude","CAP_FACE",FACE,{"disambiguationData":[OSD([sQuery(id+"F26.wireOp",EDGE,"E85.2.0.0"),sQuery(id+"F26.wireOp",EDGE,"E85.2.0.1"),sQuery(id+"F26.wireOp",EDGE,"E85.2.0.2"),sQuery(id+"F26.wireOp",EDGE,"E85.2.0.3"),sQuery(id+"F26.wireOp",EDGE,"E85.2.0.4"),sQuery(id+"F26.wireOp",EDGE,"E85.2.0.5"),sQuery(id+"F26.wireOp",EDGE,"E85.2.0.6"),sQuery(id+"F26.wireOp",EDGE,"E85.2.0.7"),sQuery(id+"F26.wireOp",EDGE,"E85.2.0.8"),sQuery(id+"F26.wireOp",EDGE,"E85.2.0.9")])],"isStart":false})});
            var Q7;
            Q7=makeQuery(id+"F27.boolean.opBoolean","COPY",FACE,{"derivedFrom":makeQuery(id+"F27.opExtrude","CAP_FACE",FACE,{"disambiguationData":[OSD([sQuery(id+"F26.wireOp",EDGE,"E86.2.0.0"),sQuery(id+"F26.wireOp",EDGE,"E86.2.0.1"),sQuery(id+"F26.wireOp",EDGE,"E86.2.0.2"),sQuery(id+"F26.wireOp",EDGE,"E86.2.0.3"),sQuery(id+"F26.wireOp",EDGE,"E86.2.0.4"),sQuery(id+"F26.wireOp",EDGE,"E86.2.0.5"),sQuery(id+"F26.wireOp",EDGE,"E86.2.0.6"),sQuery(id+"F26.wireOp",EDGE,"E86.2.0.7"),sQuery(id+"F26.wireOp",EDGE,"E86.2.0.8"),sQuery(id+"F26.wireOp",EDGE,"E86.2.0.9")])],"isStart":false})});
            var Q8;
            Q8=makeQuery(id+"F27.boolean.opBoolean","COPY",FACE,{"derivedFrom":makeQuery(id+"F27.opExtrude","CAP_FACE",FACE,{"disambiguationData":[OSD([sQuery(id+"F26.wireOp",EDGE,"E87.1.0.0"),sQuery(id+"F26.wireOp",EDGE,"E87.1.0.1"),sQuery(id+"F26.wireOp",EDGE,"E87.1.0.2"),sQuery(id+"F26.wireOp",EDGE,"E87.1.0.3"),sQuery(id+"F26.wireOp",EDGE,"E87.1.0.4"),sQuery(id+"F26.wireOp",EDGE,"E87.1.0.5"),sQuery(id+"F26.wireOp",EDGE,"E87.1.0.6"),sQuery(id+"F26.wireOp",EDGE,"E87.1.0.7"),sQuery(id+"F26.wireOp",EDGE,"E87.1.0.8"),sQuery(id+"F26.wireOp",EDGE,"E87.1.0.9")])],"isStart":false})});
            var Q9;
            Q9=makeQuery(id+"F27.boolean.opBoolean","COPY",FACE,{"derivedFrom":makeQuery(id+"F27.opExtrude","CAP_FACE",FACE,{"disambiguationData":[OSD([sQuery(id+"F26.wireOp",EDGE,"E87.2.0.0"),sQuery(id+"F26.wireOp",EDGE,"E87.2.0.1"),sQuery(id+"F26.wireOp",EDGE,"E87.2.0.2"),sQuery(id+"F26.wireOp",EDGE,"E87.2.0.3"),sQuery(id+"F26.wireOp",EDGE,"E87.2.0.4"),sQuery(id+"F26.wireOp",EDGE,"E87.2.0.5"),sQuery(id+"F26.wireOp",EDGE,"E87.2.0.6"),sQuery(id+"F26.wireOp",EDGE,"E87.2.0.7"),sQuery(id+"F26.wireOp",EDGE,"E87.2.0.8"),sQuery(id+"F26.wireOp",EDGE,"E87.2.0.9")])],"isStart":false})});
            var Q10;
            Q10=makeQuery(id+"F27.boolean.opBoolean","COPY",FACE,{"derivedFrom":makeQuery(id+"F27.opExtrude","CAP_FACE",FACE,{"disambiguationData":[OSD([sQuery(id+"F26.wireOp",EDGE,"E84.2.0.0"),sQuery(id+"F26.wireOp",EDGE,"E84.2.0.1"),sQuery(id+"F26.wireOp",EDGE,"E84.2.0.2"),sQuery(id+"F26.wireOp",EDGE,"E84.2.0.3"),sQuery(id+"F26.wireOp",EDGE,"E84.2.0.4"),sQuery(id+"F26.wireOp",EDGE,"E84.2.0.5"),sQuery(id+"F26.wireOp",EDGE,"E84.2.0.6"),sQuery(id+"F26.wireOp",EDGE,"E84.2.0.7"),sQuery(id+"F26.wireOp",EDGE,"E84.2.0.8"),sQuery(id+"F26.wireOp",EDGE,"E84.2.0.9")])],"isStart":false})});
            var Q11;
            Q11=makeQuery(id+"F27.boolean.opBoolean","COPY",FACE,{"derivedFrom":makeQuery(id+"F27.opExtrude","CAP_FACE",FACE,{"disambiguationData":[OSD([sQuery(id+"F26.wireOp",EDGE,"E84.1.0.0"),sQuery(id+"F26.wireOp",EDGE,"E84.1.0.1"),sQuery(id+"F26.wireOp",EDGE,"E84.1.0.2"),sQuery(id+"F26.wireOp",EDGE,"E84.1.0.3"),sQuery(id+"F26.wireOp",EDGE,"E84.1.0.4"),sQuery(id+"F26.wireOp",EDGE,"E84.1.0.5"),sQuery(id+"F26.wireOp",EDGE,"E84.1.0.6"),sQuery(id+"F26.wireOp",EDGE,"E84.1.0.7"),sQuery(id+"F26.wireOp",EDGE,"E84.1.0.8"),sQuery(id+"F26.wireOp",EDGE,"E84.1.0.9")])],"isStart":false})});
            var Q12;
            Q12=makeQuery(id+"F27.boolean.opBoolean","COPY",FACE,{"derivedFrom":makeQuery(id+"F27.opExtrude","CAP_FACE",FACE,{"disambiguationData":[OSD([sQuery(id+"F26.wireOp",EDGE,"E83.2.0.0"),sQuery(id+"F26.wireOp",EDGE,"E83.2.0.1"),sQuery(id+"F26.wireOp",EDGE,"E83.2.0.2"),sQuery(id+"F26.wireOp",EDGE,"E83.2.0.3"),sQuery(id+"F26.wireOp",EDGE,"E83.2.0.4"),sQuery(id+"F26.wireOp",EDGE,"E83.2.0.5"),sQuery(id+"F26.wireOp",EDGE,"E83.2.0.6"),sQuery(id+"F26.wireOp",EDGE,"E83.2.0.7"),sQuery(id+"F26.wireOp",EDGE,"E83.2.0.8"),sQuery(id+"F26.wireOp",EDGE,"E83.2.0.9")])],"isStart":false})});
            chamfer(context, id + "F31", {"entities" : qUnion([Q0, Q1, Q2, Q3, Q4, Q5, Q6, Q7, Q8, Q9, Q10, Q11, Q12]), "width" : 3.17 * mm, "tangentPropagation" : true});
        }
        {
            var Q0;
            Q0=makeQuery(id+"F25.opExtrude","CAP_EDGE",EDGE,{"disambiguationData":[OSD([sQuery(id+"F24.wireOp",EDGE,"E69")])],"isStart":false});
            var Q1;
            Q1=makeQuery(id+"F25.opExtrude","CAP_EDGE",EDGE,{"disambiguationData":[OSD([sQuery(id+"F24.wireOp",EDGE,"E68")])],"isStart":false});
            var Q2;
            Q2=makeQuery(id+"F25.opExtrude","CAP_EDGE",EDGE,{"disambiguationData":[OSD([sQuery(id+"F24.wireOp",EDGE,"E64")])],"isStart":false});
            var Q3;
            Q3=makeQuery(id+"F25.opExtrude","CAP_EDGE",EDGE,{"disambiguationData":[OSD([sQuery(id+"F24.wireOp",EDGE,"E65")])],"isStart":false});
            var Q4;
            Q4=makeQuery(id+"F25.opExtrude","CAP_EDGE",EDGE,{"disambiguationData":[OSD([sQuery(id+"F24.wireOp",EDGE,"E66")])],"isStart":false});
            var Q5;
            Q5=makeQuery(id+"F25.opExtrude","CAP_EDGE",EDGE,{"disambiguationData":[OSD([sQuery(id+"F24.wireOp",EDGE,"E67")])],"isStart":false});
            var Q6;
            Q6=makeQuery(id+"F25.opExtrude","CAP_EDGE",EDGE,{"disambiguationData":[OSD([sQuery(id+"F24.wireOp",EDGE,"E71")])],"isStart":false});
            var Q7;
            Q7=makeQuery(id+"F25.opExtrude","CAP_EDGE",EDGE,{"disambiguationData":[OSD([sQuery(id+"F24.wireOp",EDGE,"E70")])],"isStart":false});
            chamfer(context, id + "F32", {"entities" : qUnion([Q0, Q1, Q2, Q3, Q4, Q5, Q6, Q7]), "width" : 3.17 * mm, "tangentPropagation" : true});
        }
        {
            var Q0;
            Q0=makeQuery(id+"F11.boolean.opBoolean","MERGE",FACE,{"derivedFrom":[makeQuery(id+"F5.boolean.opBoolean","MERGE",FACE,{"derivedFrom":[makeQuery(id+"F3.opExtrude","SWEPT_FACE",FACE,{"disambiguationData":[OSD([sQuery(id+"F2.wireOp",EDGE,"E5.left")])]}),makeQuery(id+"F5.opExtrude","SWEPT_FACE",FACE,{"disambiguationData":[OSD([sQuery(id+"F4.wireOp",EDGE,"E12")])]})]}),makeQuery(id+"F11.opExtrude","SWEPT_FACE",FACE,{"disambiguationData":[OSD([sQuery(id+"F10.wireOp",EDGE,"E25")])]})]});
            var Q1;
            Q1=makeQuery(id+"F30.opExtrude","CAP_EDGE",EDGE,{"disambiguationData":[OSD([sQuery(id+"F29.wireOp",EDGE,"E94")])],"isStart":true});
            var Q2;
            Q2=makeQuery(id+"F30.opExtrude","SWEPT_EDGE",EDGE,{"disambiguationData":[OSD([sQuery(id+"F29.wireOp",EDGE,"E94"),sQuery(id+"F29.wireOp",EDGE,"E95")])]});
            var Q3;
            Q3=makeQuery(id+"F3.opExtrude","CAP_EDGE",EDGE,{"disambiguationData":[OSD([sQuery(id+"F2.wireOp",EDGE,"E5.top")])],"isStart":false});
            var Q4;
            Q4=makeQuery(id+"F13.boolean.opBoolean","MERGE",FACE,{"derivedFrom":[makeQuery(id+"F5.boolean.opBoolean","MERGE",FACE,{"derivedFrom":[makeQuery(id+"F3.opExtrude","SWEPT_FACE",FACE,{"disambiguationData":[OSD([sQuery(id+"F2.wireOp",EDGE,"E4.left")])]}),makeQuery(id+"F5.opExtrude","SWEPT_FACE",FACE,{"disambiguationData":[OSD([sQuery(id+"F4.wireOp",EDGE,"E8")])]})]}),makeQuery(id+"F13.opExtrude","SWEPT_FACE",FACE,{"disambiguationData":[OSD([sQuery(id+"F12.wireOp",EDGE,"E35")])]})]});
            var Q5;
            Q5=makeQuery(id+"F3.opExtrude","CAP_EDGE",EDGE,{"disambiguationData":[OSD([sQuery(id+"F2.wireOp",EDGE,"E4.top")])],"isStart":false});
            var Q6;
            Q6=makeQuery(id+"F30.opExtrude","CAP_EDGE",EDGE,{"disambiguationData":[OSD([sQuery(id+"F29.wireOp",EDGE,"E91")])],"isStart":true});
            var Q7;
            Q7=makeQuery(id+"F30.opExtrude","SWEPT_EDGE",EDGE,{"disambiguationData":[OSD([sQuery(id+"F29.wireOp",EDGE,"E90"),sQuery(id+"F29.wireOp",EDGE,"E91")])]});
            chamfer(context, id + "F33", {"entities" : qUnion([Q0, Q1, Q2, Q3, Q4, Q5, Q6, Q7]), "width" : 5.08 * mm, "tangentPropagation" : true});
        }
    });
